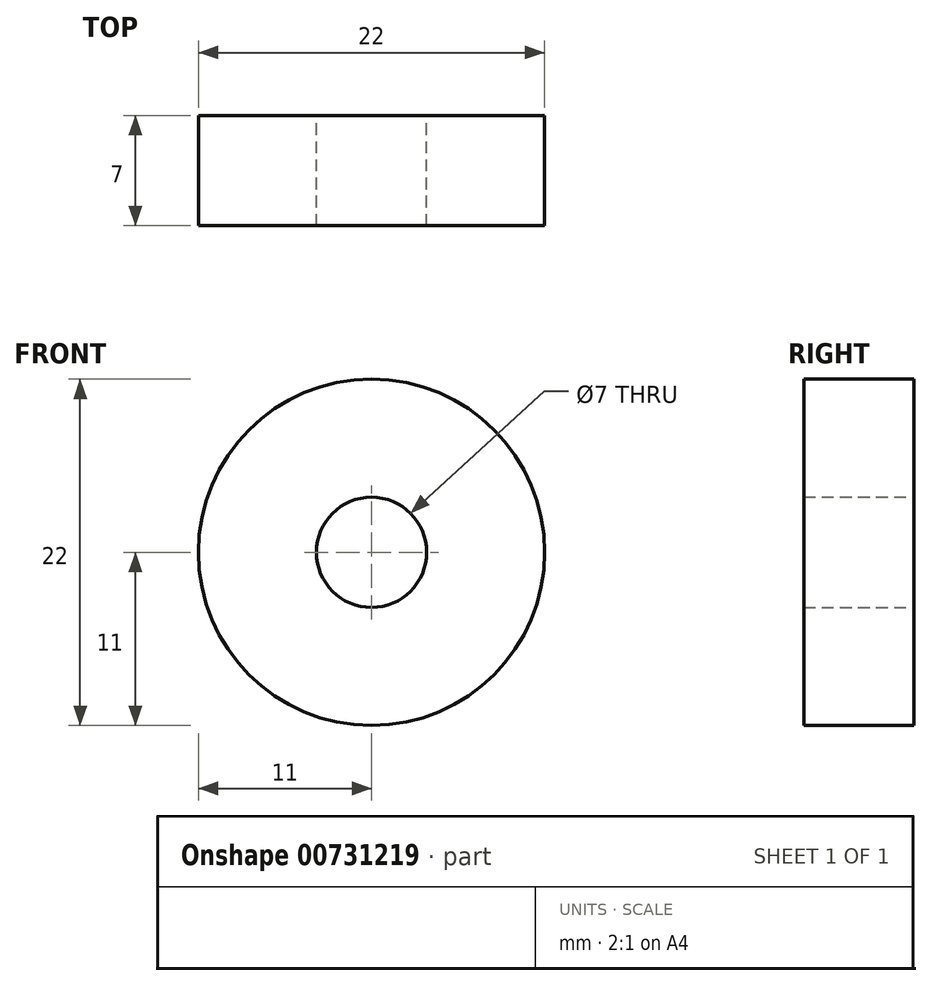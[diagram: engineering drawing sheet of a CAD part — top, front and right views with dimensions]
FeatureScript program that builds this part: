
annotation { "Feature Type Name" : "Feature", "Feature Type Description" : "" }
export const myFeature = defineFeature(function(context is Context, id is Id, definition is map)
    precondition{}
    {
        {
            var Q0;
            Q0=qCreatedBy(makeId("Front.planeOp"),FACE);
            var sketch = newSketch(context, id + "F0", { "sketchPlane" : qUnion([Q0])});
            skCircle(sketch, "E0", {"center": v(0, 0) * mm, "radius": 11 * mm});
            skCircle(sketch, "E1", {"center": v(0, 0) * mm, "radius": 3.5 * mm});
            skSolve(sketch);
        }
        {
            var Q0;
            Q0 = qSketchRegion(id + "F0", true);
            extrude(context, id + "F1", {"entities" : qUnion([Q0]), "depth" : 7 * mm, "offsetDistance" : 25.4 * mm});
        }
    });
